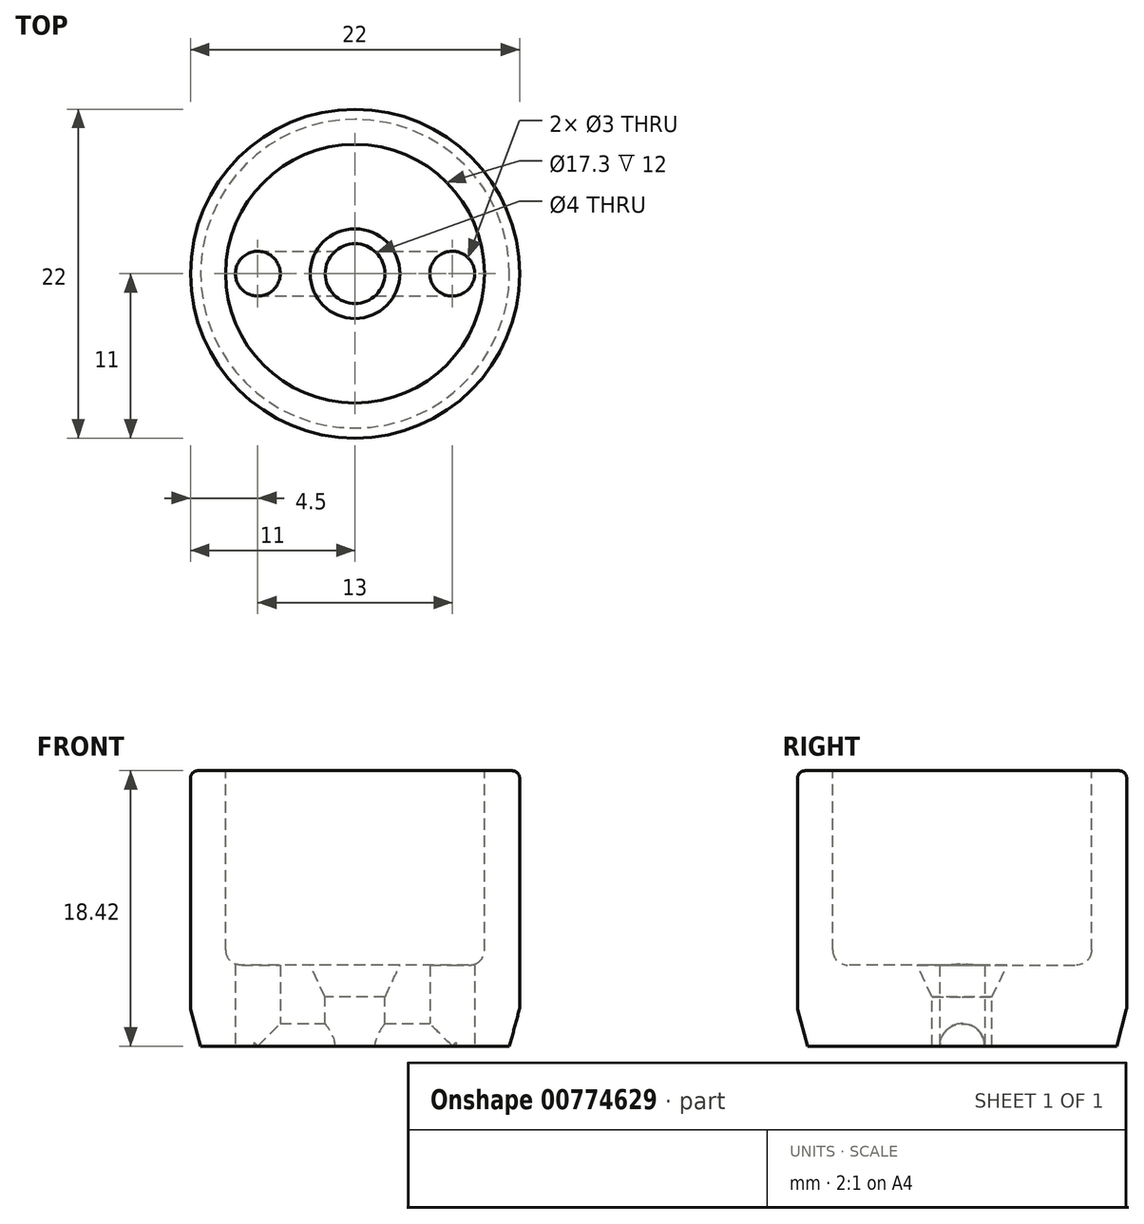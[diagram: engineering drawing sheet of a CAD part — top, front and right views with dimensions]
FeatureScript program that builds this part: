
annotation { "Feature Type Name" : "Feature", "Feature Type Description" : "" }
export const myFeature = defineFeature(function(context is Context, id is Id, definition is map)
    precondition{}
    {
        {
            var Q0;
            Q0=qCreatedBy(makeId("Front.planeOp"),FACE);
            var sketch = newSketch(context, id + "F0", { "sketchPlane" : qUnion([Q0])});
            skLineSegment(sketch, "E0", {"start": v(-11, 66) * mm, "end": v(-8.65, 66) * mm});
            skLineSegment(sketch, "E1", {"start": v(-7.65, 53) * mm, "end": v(-3, 53) * mm});
            skLineSegment(sketch, "E2", {"start": v(-8.65, 54) * mm, "end": v(-8.65, 66) * mm});
            skLineSegment(sketch, "E3", {"start": v(-3, 53) * mm, "end": v(-2, 50.86) * mm});
            skLineSegment(sketch, "E4", {"start": v(-2, 50.86) * mm, "end": v(-2, 47.58) * mm});
            skPoint(sketch, "E5.orphan", {"position": v(0, 53) * mm});
            skLineSegment(sketch, "E6", {"start": v(-8, 0) * mm, "end": v(-8, 0) * mm});
            skPoint(sketch, "E7.end.orphan", {"position": v(0, 66) * mm});
            skPoint(sketch, "E8.visualSharp", {"position": v(-10, 0) * mm});
            skPoint(sketch, "E9.visualSharp", {"position": v(-8, 0) * mm});
            skPoint(sketch, "E10.visualSharp", {"position": v(-17.5, -11) * mm});
            skLineSegment(sketch, "E11", {"start": v(0, 75.07) * mm, "end": v(0, -45.35) * mm});
            skPoint(sketch, "E12.visualSharp", {"position": v(-8.65, 53) * mm});
            skArc(sketch, "E12.filletArc", {"start": v(-8.65, 54) * mm, "mid": v(-8.36, 53.3) * mm, "end": v(-7.65, 53) * mm});
            skPoint(sketch, "E13.endSnap0", {"position": v(-2, 45.85) * mm});
            skPoint(sketch, "E14.orphan", {"position": v(-2, 40.84) * mm});
            skPoint(sketch, "E15.end.orphan", {"position": v(-24.75, -11) * mm});
            skPoint(sketch, "E16.end.orphan", {"position": v(-10, -20) * mm});
            skLineSegment(sketch, "E17", {"start": v(-8.65, 66) * mm, "end": v(-11, 66) * mm});
            skLineSegment(sketch, "E18", {"start": v(-11, 66) * mm, "end": v(-11, 50.1) * mm});
            skLineSegment(sketch, "E19", {"start": v(-11, 50.1) * mm, "end": v(-10.33, 47.58) * mm});
            skLineSegment(sketch, "E20", {"start": v(-2, 47.58) * mm, "end": v(-10.33, 47.58) * mm});
            skPoint(sketch, "E21.orphan", {"position": v(-17.5, 66) * mm});
            skPoint(sketch, "E13.end.orphan", {"position": v(-2, 45.96) * mm});
            skSolve(sketch);
        }
        {
            var Q0;
            Q0=makeQuery(id+"F0.imprint","IMPRINT",FACE,{"disambiguationData":[TD([[makeQuery(id+"F0.imprint","IMPRINT",EDGE,{"derivedFrom":sQuery(id+"F0.wireOp",EDGE,"ox1n2H6T-dIty-8iQC-gj3U-BG51KWgCMjp7")}),-1.0]])]});
            var Q1;
            Q1=makeQuery(id+"F0.imprint","IMPRINT",FACE,{"disambiguationData":[TD([[makeQuery(id+"F0.imprint","IMPRINT",EDGE,{"derivedFrom":sQuery(id+"F0.wireOp",EDGE,"E1")}),-1.0]])]});
            var Q2;
            Q2=sQuery(id+"F0.wireOp",EDGE,"E11");
            revolve(context, id + "F1", {"surfaceOperationType" : NewSurfaceOperationType.NEW, "entities" : qUnion([Q0, Q1]), "axis" : qUnion([Q2]), "revolveType" : RevolveType.FULL});
        }
        {
            var Q0;
            Q0=qCreatedBy(makeId("Top.planeOp"),FACE);
            var sketch = newSketch(context, id + "F2", { "sketchPlane" : qUnion([Q0])});
            skLineSegment(sketch, "E22", {"start": v(0, 0) * mm, "end": v(6.5, 0) * mm});
            skLineSegment(sketch, "E23", {"start": v(0, 0) * mm, "end": v(-6.5, 0) * mm});
            skCircle(sketch, "E24", {"center": v(-6.5, 0) * mm, "radius": 1.5 * mm});
            skCircle(sketch, "E25", {"center": v(6.5, 0) * mm, "radius": 1.5 * mm});
            skSolve(sketch);
        }
        {
            var Q0;
            Q0=makeQuery(id+"F2.imprint","IMPRINT",FACE,{"disambiguationData":[TD([[makeQuery(id+"F2.imprint","IMPRINT",EDGE,{"derivedFrom":sQuery(id+"F2.wireOp",EDGE,"E24")}),1.0]])]});
            var Q1;
            Q1=makeQuery(id+"F2.imprint","IMPRINT",FACE,{"disambiguationData":[TD([[makeQuery(id+"F2.imprint","IMPRINT",EDGE,{"derivedFrom":sQuery(id+"F2.wireOp",EDGE,"E25")}),1.0]])]});
            extrude(context, id + "F3", {"entities" : qUnion([Q0, Q1]), "operationType" : NewBodyOperationType.REMOVE, "depth" : 80 * mm, "offsetDistance" : 25 * mm});
        }
        {
            var Q0;
            Q0=makeQuery(id+"F1.opRevolve","SWEPT_EDGE",EDGE,{"disambiguationData":[OSD([sQuery(id+"F0.wireOp",EDGE,"E17"),sQuery(id+"F0.wireOp",EDGE,"E18")])]});
            fillet(context, id + "F4", {"entities" : qUnion([Q0]), "radius" : 0.5 * mm, "tangentPropagation" : true, "allowEdgeOverflow" : false});
        }
        {
            var Q0;
            Q0=qCreatedBy(makeId("Right.planeOp"),FACE);
            var sketch = newSketch(context, id + "F5", { "sketchPlane" : qUnion([Q0])});
            skCircle(sketch, "E26", {"center": v(0, 47.59) * mm, "radius": 1.5 * mm});
            skSolve(sketch);
        }
        {
            var Q0;
            Q0=makeQuery(id+"F5.imprint","IMPRINT",FACE,{"disambiguationData":[TD([[makeQuery(id+"F5.imprint","IMPRINT",EDGE,{"derivedFrom":sQuery(id+"F5.wireOp",EDGE,"E26")}),1.0]])]});
            extrude(context, id + "F6", {"entities" : qUnion([Q0]), "operationType" : NewBodyOperationType.REMOVE, "endBound" : BoundingType.SYMMETRIC, "oppositeDirection" : true, "depth" : 13.5 * mm, "offsetDistance" : 25 * mm});
        }
    });
